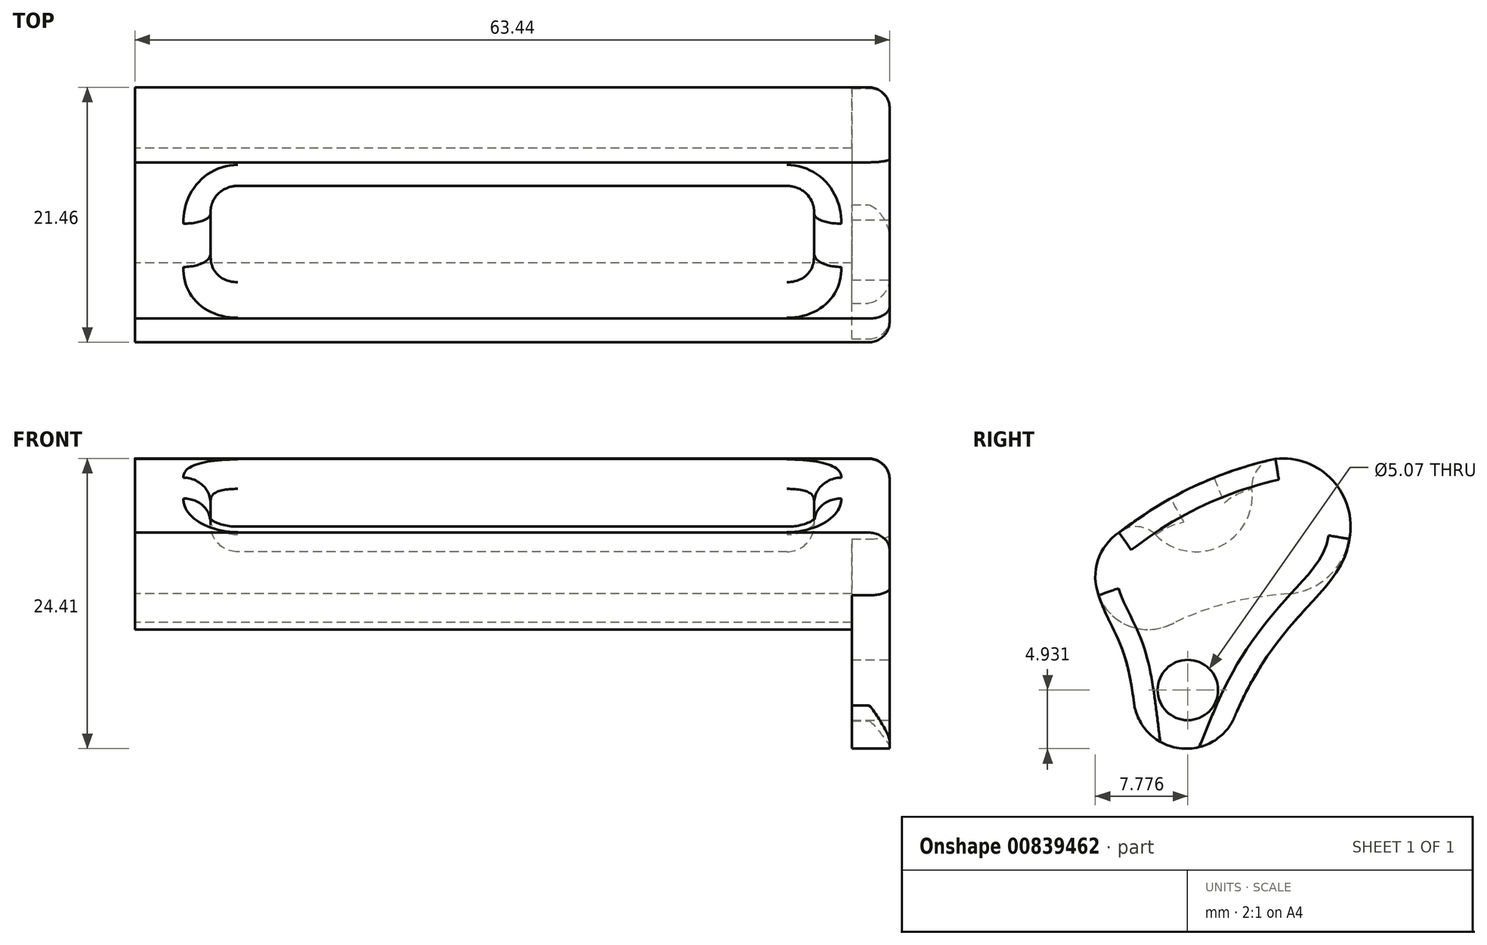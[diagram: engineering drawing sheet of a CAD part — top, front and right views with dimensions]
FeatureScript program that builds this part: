
annotation { "Feature Type Name" : "Feature", "Feature Type Description" : "" }
export const myFeature = defineFeature(function(context is Context, id is Id, definition is map)
    precondition{}
    {
        {
            var Q0;
            Q0=qCreatedBy(makeId("Right.planeOp"),FACE);
            var sketch = newSketch(context, id + "F0", { "sketchPlane" : qUnion([Q0])});
            skFitSpline(sketch, "E0.MirrorCS", {"points": [v(-24.52, 37.87) * mm, v(-37.67, 31.65) * mm], "startDerivative": vector(-20.21, -4.55) * mm, "endDerivative": vector(-7.22, -5.4) * mm});
            skArc(sketch, "E1.MirrorCS", {"start": v(-33, 24.1) * mm, "mid": v(-39, 25.6) * mm, "end": v(-37.67, 31.65) * mm});
            skFitSpline(sketch, "E2.MirrorCS", {"points": [v(-23.32, 26.5) * mm, v(-33, 24.1) * mm], "startDerivative": vector(-11.34, -0.8) * mm, "endDerivative": vector(-9.86, -4.55) * mm});
            skArc(sketch, "E3.MirrorCS", {"start": v(-24.52, 37.87) * mm, "mid": v(-18.22, 32.78) * mm, "end": v(-23.32, 26.5) * mm});
            skSolve(sketch);
        }
        {
            var Q0;
            Q0 = qSketchRegion(id + "F0", true);
            extrude(context, id + "F1", {"entities" : qUnion([Q0]), "depth" : 63.5 * mm, "offsetDistance" : 25.4 * mm});
        }
        {
            var Q0;
            Q0=makeQuery(id+"F1.opExtrude","CAP_FACE",FACE,{"disambiguationData":[OSD([sQuery(id+"F0.wireOp",EDGE,"E0.MirrorCS"),sQuery(id+"F0.wireOp",EDGE,"E1.MirrorCS"),sQuery(id+"F0.wireOp",EDGE,"E2.MirrorCS"),sQuery(id+"F0.wireOp",EDGE,"E3.MirrorCS")])],"isStart":false});
            var sketch = newSketch(context, id + "F2", { "sketchPlane" : qUnion([Q0])});
            skCircle(sketch, "E4", {"center": v(-32.01, 17.9) * mm, "radius": 4.45 * mm});
            skFitSpline(sketch, "E5", {"points": [v(-39.39, 26.37) * mm, v(-36.39, 17.1) * mm], "startDerivative": vector(3, -9.27) * mm, "endDerivative": vector(2.16, -17.37) * mm});
            skFitSpline(sketch, "E6", {"points": [v(-18.3, 31.12) * mm, v(-28.1, 15.8) * mm], "startDerivative": vector(-1.97, -14.17) * mm, "endDerivative": vector(-11.56, -28.1) * mm});
            skSolve(sketch);
        }
        {
            var Q0;
            {var subQ5=makeQuery(id+"F1.opExtrude","CAP_EDGE",EDGE,{"disambiguationData":[OSD([sQuery(id+"F0.wireOp",EDGE,"E2.MirrorCS")])],"isStart":false});Q0=makeQuery(id+"F2.imprint","IMPRINT",FACE,{"disambiguationData":[TD([[makeQuery(id+"F2.imprint","IMPRINT",EDGE,{"derivedFrom":subQ5}),1.0]])]});}
            var Q1;
            {var subQ0=sQuery(id+"F2.wireOp",EDGE,"E5");var subQ1=sQuery(id+"F2.wireOp",EDGE,"E4");var subQ2=makeQuery(id+"F2.imprint","INTERSECT",VERTEX,{"disambiguationData":[OD(0.0)],"derivedFrom":[subQ1,subQ0]});Q1=makeQuery(id+"F2.imprint","IMPRINT",FACE,{"disambiguationData":[TD([[makeQuery(id+"F2.imprint","IMPRINT",EDGE,{"disambiguationData":[TD([[subQ2,-1.0]])],"derivedFrom":subQ1}),1.0]])]});}
            extrude(context, id + "F3", {"entities" : qUnion([Q0, Q1]), "operationType" : NewBodyOperationType.ADD, "oppositeDirection" : true, "depth" : 3.17 * mm, "offsetDistance" : 25.4 * mm});
        }
        {
            var Q0;
            {var subQ0=sQuery(id+"F0.wireOp",EDGE,"E3.MirrorCS");var subQ1=sQuery(id+"F0.wireOp",EDGE,"E2.MirrorCS");var subQ2=sQuery(id+"F0.wireOp",EDGE,"E1.MirrorCS");Q0=makeQuery(id+"F3.boolean.opBoolean","MERGE",FACE,{"derivedFrom":[makeQuery(id+"F1.opExtrude","CAP_FACE",FACE,{"disambiguationData":[OSD([sQuery(id+"F0.wireOp",EDGE,"E0.MirrorCS"),subQ2,subQ1,subQ0])],"isStart":false}),makeQuery(id+"F3.opExtrude","CAP_FACE",FACE,{"disambiguationData":[OSD([subQ2,subQ1,subQ0,sQuery(id+"F2.wireOp",EDGE,"E4"),sQuery(id+"F2.wireOp",EDGE,"E5"),sQuery(id+"F2.wireOp",EDGE,"E6")])],"isStart":true})]});}
            var sketch = newSketch(context, id + "F4", { "sketchPlane" : qUnion([Q0])});
            skCircle(sketch, "E7", {"center": v(-31.9, 18.4) * mm, "radius": 2.54 * mm});
            skSolve(sketch);
        }
        {
            var Q0;
            Q0=makeQuery(id+"F4.imprint","IMPRINT",FACE,{"disambiguationData":[TD([[makeQuery(id+"F4.imprint","IMPRINT",EDGE,{"derivedFrom":sQuery(id+"F4.wireOp",EDGE,"E7")}),1.0]])]});
            extrude(context, id + "F5", {"entities" : qUnion([Q0]), "operationType" : NewBodyOperationType.REMOVE, "endBound" : BoundingType.THROUGH_ALL, "oppositeDirection" : true, "depth" : 25.4 * mm, "offsetDistance" : 25.4 * mm});
        }
        {
            var Q0;
            {var subQ0=sQuery(id+"F0.wireOp",EDGE,"E3.MirrorCS");var subQ1=sQuery(id+"F0.wireOp",EDGE,"E2.MirrorCS");var subQ2=sQuery(id+"F0.wireOp",EDGE,"E1.MirrorCS");Q0=makeQuery(id+"F3.boolean.opBoolean","MERGE",FACE,{"derivedFrom":[makeQuery(id+"F1.opExtrude","CAP_FACE",FACE,{"disambiguationData":[OSD([sQuery(id+"F0.wireOp",EDGE,"E0.MirrorCS"),subQ2,subQ1,subQ0])],"isStart":false}),makeQuery(id+"F3.opExtrude","CAP_FACE",FACE,{"disambiguationData":[OSD([subQ2,subQ1,subQ0,sQuery(id+"F2.wireOp",EDGE,"E4"),sQuery(id+"F2.wireOp",EDGE,"E5"),sQuery(id+"F2.wireOp",EDGE,"E6")])],"isStart":true})]});}
            cPlane(context, id + "F6", {"entities" : qUnion([Q0]), "cplaneType" : CPlaneType.OFFSET, "offset" : 31.75 * mm, "oppositeDirection" : true, "width" : 152.4 * mm, "height" : 152.4 * mm});
        }
        {
            var Q0;
            Q0=qCreatedBy(id+"F6.planeOp",FACE);
            var sketch = newSketch(context, id + "F7", { "sketchPlane" : qUnion([Q0])});
            skCircle(sketch, "E8", {"center": v(-31.22, 34.8) * mm, "radius": 4.76 * mm});
            skSolve(sketch);
        }
        {
            var Q0;
            Q0 = qSketchRegion(id + "F7", true);
            extrude(context, id + "F8", {"entities" : qUnion([Q0]), "operationType" : NewBodyOperationType.REMOVE, "depth" : 50.8 * mm, "offsetDistance" : 25.4 * mm, "symmetric" : true});
        }
        {
            var Q0;
            Q0=makeQuery(id+"F8.boolean.opBoolean","INTERSECT",EDGE,{"disambiguationData":[OD(1.0)],"derivedFrom":[makeQuery(id+"F1.opExtrude","SWEPT_FACE",FACE,{"disambiguationData":[OSD([sQuery(id+"F0.wireOp",EDGE,"E0.MirrorCS")])]}),makeQuery(id+"F8.opExtrude","SWEPT_FACE",FACE,{"disambiguationData":[OSD([sQuery(id+"F7.wireOp",EDGE,"E8")])]})]});
            var Q1;
            Q1=makeQuery(id+"F8.boolean.opBoolean","INTERSECT",EDGE,{"disambiguationData":[OD(0.0)],"derivedFrom":[makeQuery(id+"F1.opExtrude","SWEPT_FACE",FACE,{"disambiguationData":[OSD([sQuery(id+"F0.wireOp",EDGE,"E0.MirrorCS")])]}),makeQuery(id+"F8.opExtrude","SWEPT_FACE",FACE,{"disambiguationData":[OSD([sQuery(id+"F7.wireOp",EDGE,"E8")])]})]});
            var Q2;
            Q2=makeQuery(id+"F8.boolean.opBoolean","INTERSECT",EDGE,{"derivedFrom":[makeQuery(id+"F1.opExtrude","SWEPT_FACE",FACE,{"disambiguationData":[OSD([sQuery(id+"F0.wireOp",EDGE,"E0.MirrorCS")])]}),makeQuery(id+"F8.opExtrude","CAP_FACE",FACE,{"disambiguationData":[OSD([sQuery(id+"F7.wireOp",EDGE,"E8")])],"isStart":true})]});
            var Q3;
            Q3=makeQuery(id+"F8.boolean.opBoolean","INTERSECT",EDGE,{"derivedFrom":[makeQuery(id+"F1.opExtrude","SWEPT_FACE",FACE,{"disambiguationData":[OSD([sQuery(id+"F0.wireOp",EDGE,"E0.MirrorCS")])]}),makeQuery(id+"F8.opExtrude","CAP_FACE",FACE,{"disambiguationData":[OSD([sQuery(id+"F7.wireOp",EDGE,"E8")])],"isStart":false})]});
            var Q4;
            Q4=makeQuery(id+"F8.boolean.opBoolean","COPY",EDGE,{"derivedFrom":makeQuery(id+"F8.opExtrude","CAP_EDGE",EDGE,{"disambiguationData":[OSD([sQuery(id+"F7.wireOp",EDGE,"E8")])],"isStart":true})});
            var Q5;
            Q5=makeQuery(id+"F8.boolean.opBoolean","COPY",EDGE,{"derivedFrom":makeQuery(id+"F8.opExtrude","CAP_EDGE",EDGE,{"disambiguationData":[OSD([sQuery(id+"F7.wireOp",EDGE,"E8")])],"isStart":false})});
            fillet(context, id + "F9", {"entities" : qUnion([Q0, Q1, Q2, Q3, Q4, Q5]), "radius" : 2.3 * mm, "tangentPropagation" : true, "allowEdgeOverflow" : false});
        }
        {
            var Q0;
            Q0=makeQuery(id+"F1.opExtrude","SWEPT_BODY",BODY,{"disambiguationData":[OSD([sQuery(id+"F0.wireOp",EDGE,"E0.MirrorCS"),sQuery(id+"F0.wireOp",EDGE,"E1.MirrorCS"),sQuery(id+"F0.wireOp",EDGE,"E2.MirrorCS"),sQuery(id+"F0.wireOp",EDGE,"E3.MirrorCS")])]});
            var Q1;
            Q1=makeQuery(id+"F1.opExtrude","CAP_VERTEX",VERTEX,{"disambiguationData":[OSD([sQuery(id+"F0.wireOp",EDGE,"E0.MirrorCS"),sQuery(id+"F0.wireOp",EDGE,"E3.MirrorCS")])],"isStart":true});
            transform(context, id + "F10", {"entities" : qUnion([Q0]), "transformType" : TransformType.SCALE_UNIFORMLY, "scale" : .999, "scalePoint" : qUnion([Q1]), "makeCopy" : false});
        }
        {
            var Q0;
            Q0=makeQuery(id+"F1.opExtrude","CAP_EDGE",EDGE,{"disambiguationData":[OSD([sQuery(id+"F0.wireOp",EDGE,"E0.MirrorCS")])],"isStart":false});
            var Q1;
            Q1=makeQuery(id+"F1.opExtrude","CAP_EDGE",EDGE,{"disambiguationData":[OSD([sQuery(id+"F0.wireOp",EDGE,"E1.MirrorCS")])],"isStart":false});
            var Q2;
            Q2=makeQuery(id+"F1.opExtrude","CAP_EDGE",EDGE,{"disambiguationData":[OSD([sQuery(id+"F0.wireOp",EDGE,"E3.MirrorCS")])],"isStart":false});
            fillet(context, id + "F11", {"entities" : qUnion([Q0, Q1, Q2]), "radius" : 1.78 * mm, "tangentPropagation" : true, "allowEdgeOverflow" : false});
        }
    });
